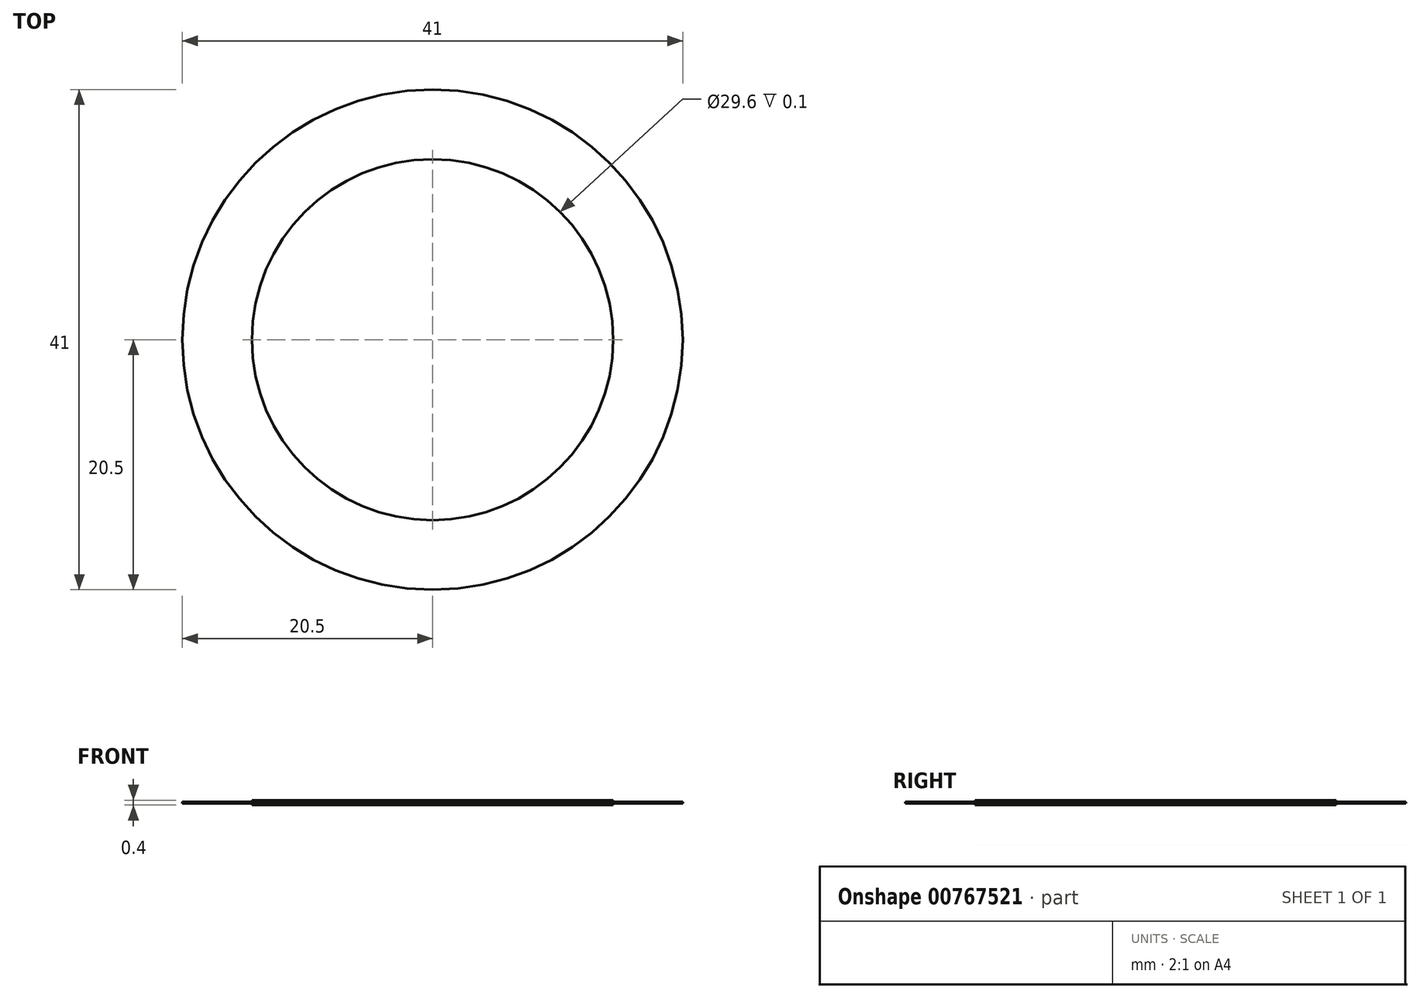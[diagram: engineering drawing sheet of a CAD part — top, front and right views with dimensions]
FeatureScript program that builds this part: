
annotation { "Feature Type Name" : "Feature", "Feature Type Description" : "" }
export const myFeature = defineFeature(function(context is Context, id is Id, definition is map)
    precondition{}
    {
        {
            var Q0;
            Q0=qCreatedBy(makeId("Top.planeOp"),FACE);
            var sketch = newSketch(context, id + "F0", { "sketchPlane" : qUnion([Q0])});
            skCircle(sketch, "E0", {"center": v(0, 0) * mm, "radius": 20.5 * mm});
            skCircle(sketch, "E1", {"center": v(0, 0) * mm, "radius": 14.8 * mm});
            skSolve(sketch);
        }
        {
            var Q0;
            Q0=makeQuery(id+"F0.imprint","IMPRINT",FACE,{"disambiguationData":[TD([[makeQuery(id+"F0.imprint","IMPRINT",EDGE,{"derivedFrom":sQuery(id+"F0.wireOp",EDGE,"E1")}),1.0]])]});
            extrude(context, id + "F1", {"entities" : qUnion([Q0]), "endBound" : BoundingType.SYMMETRIC, "depth" : 0.4 * mm, "offsetDistance" : 25 * mm});
        }
        {
            var Q0;
            Q0=makeQuery(id+"F0.imprint","IMPRINT",FACE,{"disambiguationData":[TD([[makeQuery(id+"F0.imprint","IMPRINT",EDGE,{"derivedFrom":sQuery(id+"F0.wireOp",EDGE,"E0")}),1.0]])]});
            extrude(context, id + "F2", {"entities" : qUnion([Q0]), "endBound" : BoundingType.SYMMETRIC, "depth" : 0.1 * mm, "offsetDistance" : 25 * mm});
        }
    });
